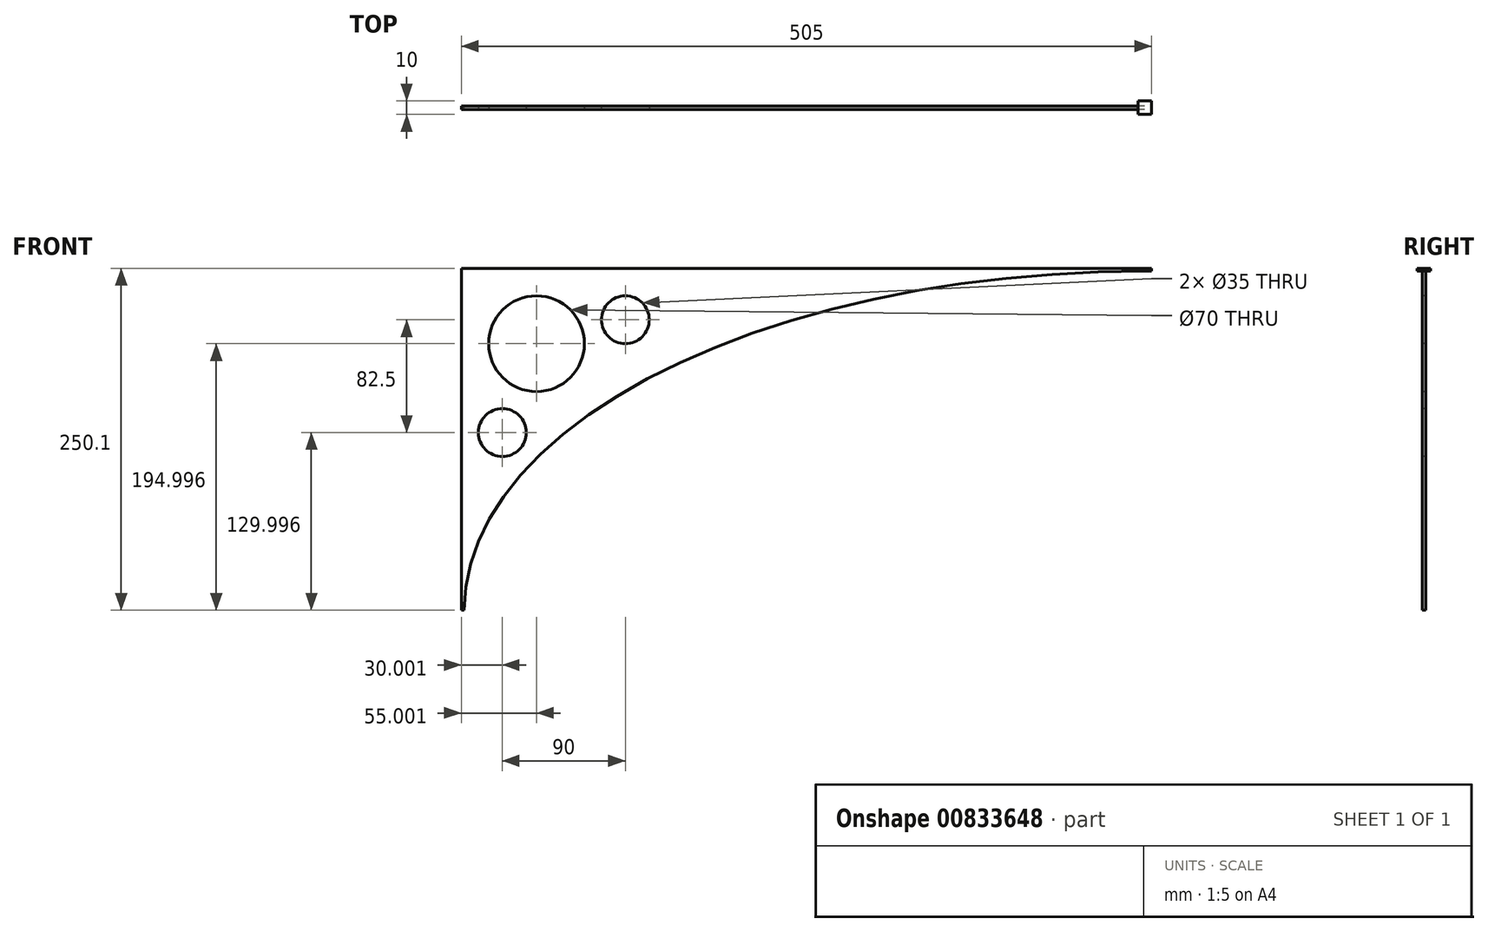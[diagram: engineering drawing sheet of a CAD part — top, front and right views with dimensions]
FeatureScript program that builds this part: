
annotation { "Feature Type Name" : "Feature", "Feature Type Description" : "" }
export const myFeature = defineFeature(function(context is Context, id is Id, definition is map)
    precondition{}
    {
        {
            var Q0;
            Q0=qCreatedBy(makeId("Front.planeOp"),FACE);
            var sketch = newSketch(context, id + "F0", { "sketchPlane" : qUnion([Q0])});
            skLineSegment(sketch, "E0", {"start": v(-265.69, 164.73) * mm, "end": v(234.31, 164.73) * mm});
            skLineSegment(sketch, "E1", {"start": v(234.31, 164.73) * mm, "end": v(234.31, 162.73) * mm});
            skLineSegment(sketch, "E2", {"start": v(-265.69, 164.73) * mm, "end": v(-265.69, -85.27) * mm});
            skLineSegment(sketch, "E3", {"start": v(-265.69, -85.27) * mm, "end": v(-263.69, -85.27) * mm});
            skEllipticalArc(sketch, "E4", {});
            const initialGuessF0  = {"E4": [0.2343109268695116, -0.08527348190546036, -1, 0, 0.498, 0.248, 4.71238898038469, 0]};
            skSetInitialGuess(sketch, initialGuessF0);
            skSolve(sketch);
        }
        {
            var Q0;
            Q0=makeQuery(id+"F0.imprint","IMPRINT",FACE,{"disambiguationData":[TD([[makeQuery(id+"F0.imprint","IMPRINT",EDGE,{"derivedFrom":sQuery(id+"F0.wireOp",EDGE,"E0")}),-1.0]])]});
            extrude(context, id + "F1", {"entities" : qUnion([Q0]), "depth" : 2.5 * mm, "offsetDistance" : 25 * mm});
        }
        {
            var Q0;
            Q0=makeQuery(id+"F1.opExtrude","CAP_FACE",FACE,{"disambiguationData":[OSD([sQuery(id+"F0.wireOp",EDGE,"E0"),sQuery(id+"F0.wireOp",EDGE,"E1"),sQuery(id+"F0.wireOp",EDGE,"E2"),sQuery(id+"F0.wireOp",EDGE,"E3"),sQuery(id+"F0.wireOp",EDGE,"E4")])],"isStart":false});
            var sketch = newSketch(context, id + "F2", { "sketchPlane" : qUnion([Q0])});
            skCircle(sketch, "E5", {"center": v(-210.69, 109.73) * mm, "radius": 35 * mm});
            skCircle(sketch, "E6", {"center": v(-145.69, 127.23) * mm, "radius": 17.5 * mm});
            skLineSegment(sketch, "E7", {"start": v(-210.69, 109.73) * mm, "end": v(-210.69, 164.73) * mm});
            skCircle(sketch, "E8", {"center": v(-235.69, 44.73) * mm, "radius": 17.5 * mm});
            skLineSegment(sketch, "E9", {"start": v(-210.69, 109.73) * mm, "end": v(-265.69, 109.73) * mm});
            skSolve(sketch);
        }
        {
            var Q0;
            Q0=sQuery(id+"F2.wireOp",VERTEX,"E5.center");
            var Q1;
            Q1=makeQuery(id+"F1.opExtrude","SWEPT_BODY",BODY,{"disambiguationData":[OSD([sQuery(id+"F0.wireOp",EDGE,"E0"),sQuery(id+"F0.wireOp",EDGE,"E1"),sQuery(id+"F0.wireOp",EDGE,"E2"),sQuery(id+"F0.wireOp",EDGE,"E3"),sQuery(id+"F0.wireOp",EDGE,"E4")])]});
            hole(context, id + "F3", {"style" : HoleStyle.SIMPLE, "endStyle" : HoleEndStyle.THROUGH, "holeDiameter" : 70 * mm, "majorDiameter" : 5 * mm, "isTappedThrough" : true, "tappedDepth" : 12 * mm, "tapClearance" : 3, "locations" : qUnion([Q0]), "scope" : qUnion([Q1])});
        }
        {
            var Q0;
            Q0=sQuery(id+"F2.wireOp",VERTEX,"E6.center");
            var Q1;
            Q1=sQuery(id+"F2.wireOp",VERTEX,"E8.center");
            var Q2;
            Q2=makeQuery(id+"F1.opExtrude","SWEPT_BODY",BODY,{"disambiguationData":[OSD([sQuery(id+"F0.wireOp",EDGE,"E0"),sQuery(id+"F0.wireOp",EDGE,"E1"),sQuery(id+"F0.wireOp",EDGE,"E2"),sQuery(id+"F0.wireOp",EDGE,"E3"),sQuery(id+"F0.wireOp",EDGE,"E4")])]});
            hole(context, id + "F4", {"style" : HoleStyle.SIMPLE, "endStyle" : HoleEndStyle.THROUGH, "holeDiameter" : 35 * mm, "majorDiameter" : 5 * mm, "isTappedThrough" : true, "tappedDepth" : 12 * mm, "tapClearance" : 3, "locations" : qUnion([Q0, Q1]), "scope" : qUnion([Q2])});
        }
        {
            var Q0;
            Q0=makeQuery(id+"F1.opExtrude","SWEPT_FACE",FACE,{"disambiguationData":[OSD([sQuery(id+"F0.wireOp",EDGE,"E0")])]});
            var sketch = newSketch(context, id + "F5", { "sketchPlane" : qUnion([Q0])});
            skLineSegment(sketch, "E10.bottom", {"start": v(239.31, 3.75) * mm, "end": v(229.31, 3.75) * mm});
            skLineSegment(sketch, "E10.top", {"start": v(239.31, -6.25) * mm, "end": v(229.31, -6.25) * mm});
            skLineSegment(sketch, "E10.left", {"start": v(239.31, 3.75) * mm, "end": v(239.31, -6.25) * mm});
            skLineSegment(sketch, "E10.right", {"start": v(229.31, 3.75) * mm, "end": v(229.31, -6.25) * mm});
            skPoint(sketch, "E10.middle", {"position": v(234.31, -1.25) * mm});
            skLineSegment(sketch, "E11", {"start": v(234.31, 0) * mm, "end": v(229.31, 0) * mm});
            skLineSegment(sketch, "E12", {"start": v(234.31, 0) * mm, "end": v(234.31, -2.5) * mm});
            skLineSegment(sketch, "E13", {"start": v(234.31, -2.5) * mm, "end": v(229.31, -2.5) * mm});
            skLineSegment(sketch, "E14", {"start": v(229.31, -2.5) * mm, "end": v(229.31, -6.25) * mm});
            skSolve(sketch);
        }
        {
            var Q0;
            {var subQ1=sQuery(id+"F5.wireOp",EDGE,"E10.bottom");Q0=makeQuery(id+"F5.imprint","IMPRINT",FACE,{"disambiguationData":[TD([[makeQuery(id+"F5.imprint","IMPRINT",EDGE,{"derivedFrom":subQ1}),1.0]])]});}
            var Q1;
            {var subQ3=sQuery(id+"F5.wireOp",EDGE,"E11");Q1=makeQuery(id+"F5.imprint","IMPRINT",FACE,{"disambiguationData":[TD([[makeQuery(id+"F5.imprint","IMPRINT",EDGE,{"derivedFrom":subQ3}),-1.0]])]});}
            extrude(context, id + "F6", {"entities" : qUnion([Q0, Q1]), "operationType" : NewBodyOperationType.ADD, "oppositeDirection" : true, "depth" : 2 * mm, "offsetDistance" : 25 * mm});
        }
        {
            var Q0;
            {var subQ1=sQuery(id+"F5.wireOp",EDGE,"E10.bottom");Q0=makeQuery(id+"F5.imprint","IMPRINT",FACE,{"disambiguationData":[TD([[makeQuery(id+"F5.imprint","IMPRINT",EDGE,{"derivedFrom":subQ1}),1.0]])]});}
            var Q1;
            {var subQ3=sQuery(id+"F5.wireOp",EDGE,"E11");Q1=makeQuery(id+"F5.imprint","IMPRINT",FACE,{"disambiguationData":[TD([[makeQuery(id+"F5.imprint","IMPRINT",EDGE,{"derivedFrom":subQ3}),-1.0]])]});}
            extrude(context, id + "F7", {"entities" : qUnion([Q0, Q1]), "operationType" : NewBodyOperationType.ADD, "depth" : 0.1 * mm, "offsetDistance" : 25 * mm});
        }
    });
